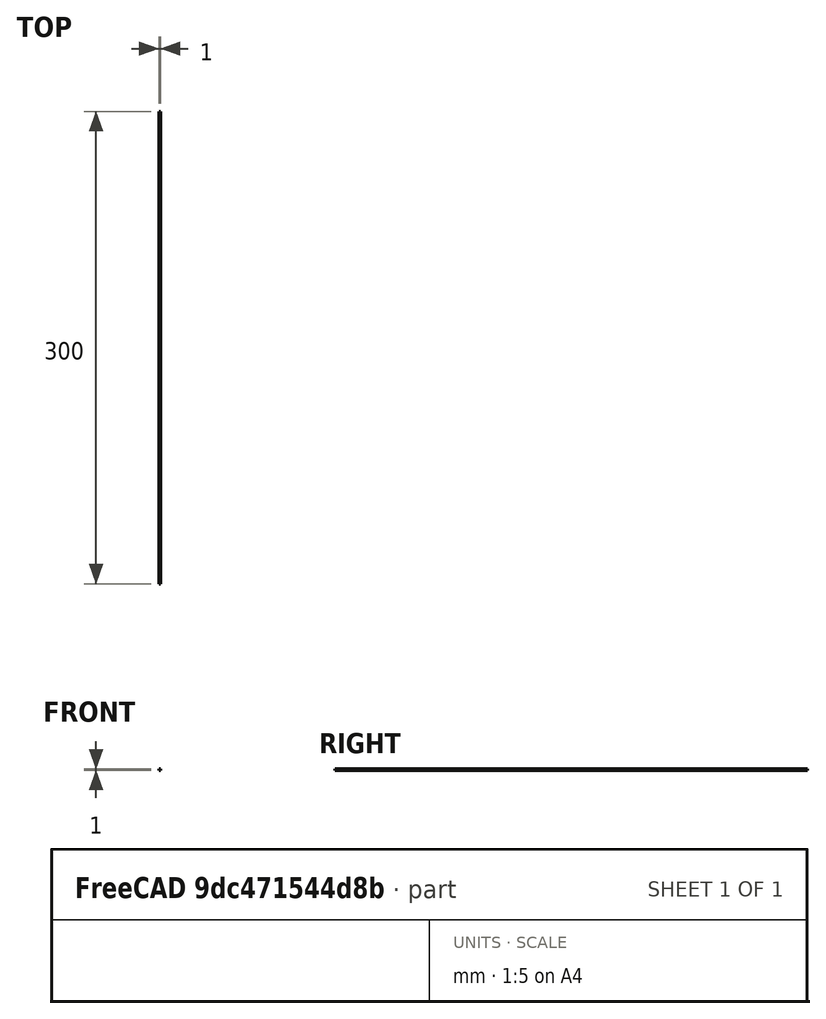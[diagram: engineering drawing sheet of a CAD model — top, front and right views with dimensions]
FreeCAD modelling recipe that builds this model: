
FCSTD DOCUMENT  (FreeCAD 0.18R16110 (Git))
Label: prutok_blue
License: All rights reserved
LicenseURL: http://en.wikipedia.org/wiki/All_rights_reserved
objects: Sketcher::SketchObject×1, PartDesign::Pad×1, PartDesign::Body×1
note: 4 computed .brp shape members not serialized (recipe doc carries the construction recipe); baked Part::Feature solids carry a one-line shape summary decoded from their .brp

FEATURE [Sketcher::SketchObject] Sketch
  MapMode = 5
  Placement = pos=(0,0,0) rot=(1,0,0;1.5708rad)
  Support = -> [XZ_Plane]
  sketch-geometry (4):
    g0: LineSegment StartX=0 StartY=0 StartZ=0 EndX=1 EndY=0 EndZ=0
    g1: LineSegment StartX=1 StartY=0 StartZ=0 EndX=1 EndY=1 EndZ=0
    g2: LineSegment StartX=1 StartY=1 StartZ=0 EndX=0 EndY=1 EndZ=0
    g3: LineSegment StartX=0 StartY=1 StartZ=0 EndX=0 EndY=0 EndZ=0
  constraints (11):
    c: Coincident(g0,g1)
    c: Coincident(g1,g2)
    c: Coincident(g2,g3)
    c: Coincident(g3,g0)
    c: Horizontal(g0)
    c: Horizontal(g2)
    c: Vertical(g1)
    c: Vertical(g3)
    c: DistanceX(g2,g2) = 1
    c: DistanceY(g1,g1) = 1
    c: Coincident(g0,g-1)
FEATURE [PartDesign::Pad] Pad
  Length = 300
  Length2 = 100
  Placement = pos=(0,0,0) rot=(1,0,0;1.5708rad)
  Profile = -> Sketch
  Type = 0
FEATURE [PartDesign::Body] Body
  Group = -> [Sketch,Pad]
  Origin = -> Origin
  Tip = -> Pad
